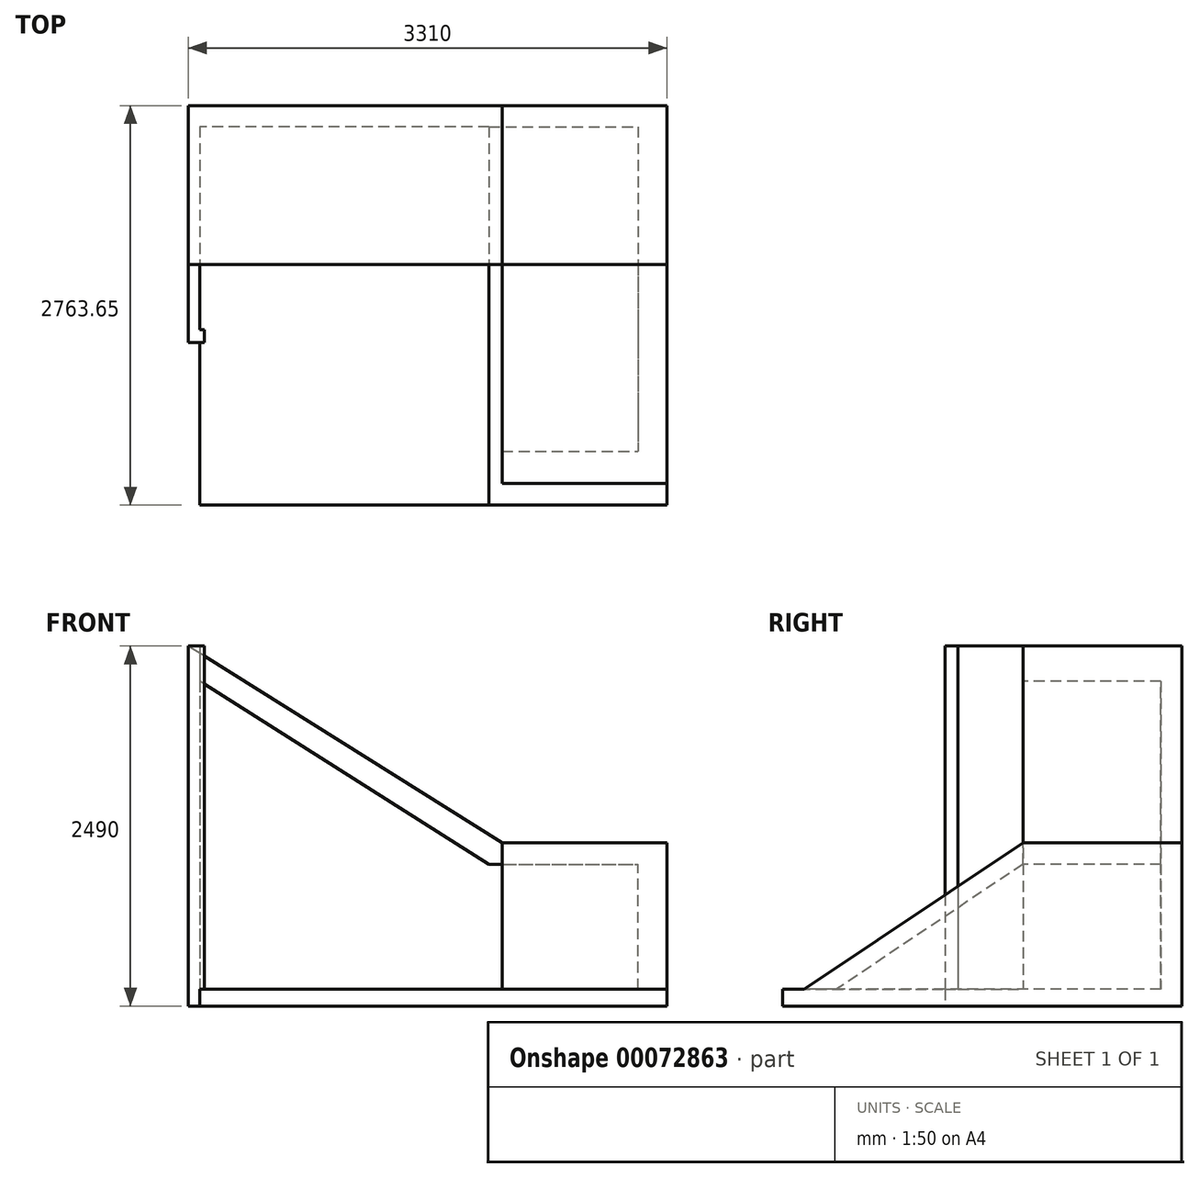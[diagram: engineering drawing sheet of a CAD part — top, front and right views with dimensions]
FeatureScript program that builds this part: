
annotation { "Feature Type Name" : "Feature", "Feature Type Description" : "" }
export const myFeature = defineFeature(function(context is Context, id is Id, definition is map)
    precondition{}
    {
        {
            var Q0;
            Q0=qCreatedBy(makeId("Front.planeOp"),FACE);
            var sketch = newSketch(context, id + "F0", { "sketchPlane" : qUnion([Q0])});
            skLineSegment(sketch, "E0", {"start": v(0, 0) * mm, "end": v(0, -2490) * mm});
            skLineSegment(sketch, "E1", {"start": v(0, -2490) * mm, "end": v(2170, -2490) * mm});
            skLineSegment(sketch, "E2", {"start": v(2170, -2490) * mm, "end": v(2170, -1360) * mm});
            skLineSegment(sketch, "E3", {"start": v(2170, -1360) * mm, "end": v(0, 0) * mm});
            skSolve(sketch);
        }
        {
            var Q0;
            Q0=makeQuery(id+"F0.imprint","IMPRINT",FACE,{"disambiguationData":[TD([[makeQuery(id+"F0.imprint","IMPRINT",EDGE,{"derivedFrom":sQuery(id+"F0.wireOp",EDGE,"E0")}),1.0]])]});
            extrude(context, id + "F1", {"entities" : qUnion([Q0]), "depth" : 1100 * mm});
        }
        {
            var Q0;
            Q0=makeQuery(id+"F1.opExtrude","CAP_FACE",FACE,{"disambiguationData":[OSD([sQuery(id+"F0.wireOp",EDGE,"E0"),sQuery(id+"F0.wireOp",EDGE,"E1"),sQuery(id+"F0.wireOp",EDGE,"E2"),sQuery(id+"F0.wireOp",EDGE,"E3")])],"isStart":false});
            var sketch = newSketch(context, id + "F2", { "sketchPlane" : qUnion([Q0])});
            skLineSegment(sketch, "E4", {"start": v(79.81, -244.3) * mm, "end": v(79.81, -2374.3) * mm});
            skLineSegment(sketch, "E5", {"start": v(79.81, -2374.3) * mm, "end": v(2079.81, -2374.3) * mm});
            skLineSegment(sketch, "E6", {"start": v(2079.81, -2374.3) * mm, "end": v(2079.81, -1509.3) * mm});
            skLineSegment(sketch, "E7", {"start": v(2079.81, -1509.3) * mm, "end": v(79.81, -244.3) * mm});
            skSolve(sketch);
        }
        {
            var Q0;
            Q0=makeQuery(id+"F2.imprint","IMPRINT",FACE,{"disambiguationData":[TD([[makeQuery(id+"F2.imprint","IMPRINT",EDGE,{"derivedFrom":sQuery(id+"F2.wireOp",EDGE,"E4")}),1.0]])]});
            extrude(context, id + "F3", {"entities" : qUnion([Q0]), "operationType" : NewBodyOperationType.REMOVE, "oppositeDirection" : true, "depth" : 955 * mm});
        }
        {
            var Q0;
            Q0=makeQuery(id+"F1.opExtrude","SWEPT_FACE",FACE,{"disambiguationData":[OSD([sQuery(id+"F0.wireOp",EDGE,"E0")])]});
            var sketch = newSketch(context, id + "F4", { "sketchPlane" : qUnion([Q0])});
            skLineSegment(sketch, "E8.bottom", {"start": v(1100, 0) * mm, "end": v(1550, 0) * mm});
            skLineSegment(sketch, "E8.top", {"start": v(1100, -2490) * mm, "end": v(1550, -2490) * mm});
            skLineSegment(sketch, "E8.left", {"start": v(1100, 0) * mm, "end": v(1100, -2490) * mm});
            skLineSegment(sketch, "E8.right", {"start": v(1550, 0) * mm, "end": v(1550, -2490) * mm});
            skSolve(sketch);
        }
        {
            var Q0;
            Q0=makeQuery(id+"F4.imprint","IMPRINT",FACE,{"disambiguationData":[TD([[makeQuery(id+"F4.imprint","IMPRINT",EDGE,{"derivedFrom":sQuery(id+"F4.wireOp",EDGE,"E8.bottom")}),-1.0]])]});
            extrude(context, id + "F5", {"entities" : qUnion([Q0]), "operationType" : NewBodyOperationType.ADD, "oppositeDirection" : true, "depth" : 80 * mm});
        }
        {
            var Q0;
            Q0=makeQuery(id+"F5.boolean.opBoolean","MERGE",FACE,{"derivedFrom":[makeQuery(id+"F1.opExtrude","SWEPT_FACE",FACE,{"disambiguationData":[OSD([sQuery(id+"F0.wireOp",EDGE,"E0")])]}),makeQuery(id+"F5.opExtrude","CAP_FACE",FACE,{"disambiguationData":[OSD([sQuery(id+"F4.wireOp",EDGE,"E8.bottom"),sQuery(id+"F4.wireOp",EDGE,"E8.top"),sQuery(id+"F4.wireOp",EDGE,"E8.left"),sQuery(id+"F4.wireOp",EDGE,"E8.right")])],"isStart":true})]});
            var sketch = newSketch(context, id + "F6", { "sketchPlane" : qUnion([Q0])});
            skLineSegment(sketch, "E9.bottom", {"start": v(1550, 0) * mm, "end": v(1640, 0) * mm});
            skLineSegment(sketch, "E9.top", {"start": v(1550, -2490) * mm, "end": v(1640, -2490) * mm});
            skLineSegment(sketch, "E9.left", {"start": v(1550, 0) * mm, "end": v(1550, -2490) * mm});
            skLineSegment(sketch, "E9.right", {"start": v(1640, 0) * mm, "end": v(1640, -2490) * mm});
            skSolve(sketch);
        }
        {
            var Q0;
            Q0=makeQuery(id+"F6.imprint","IMPRINT",FACE,{"disambiguationData":[TD([[makeQuery(id+"F6.imprint","IMPRINT",EDGE,{"derivedFrom":sQuery(id+"F6.wireOp",EDGE,"E9.bottom")}),-1.0]])]});
            extrude(context, id + "F7", {"entities" : qUnion([Q0]), "operationType" : NewBodyOperationType.ADD, "oppositeDirection" : true, "depth" : 110 * mm});
        }
        {
            var Q0;
            Q0=makeQuery(id+"F1.opExtrude","CAP_FACE",FACE,{"disambiguationData":[OSD([sQuery(id+"F0.wireOp",EDGE,"E0"),sQuery(id+"F0.wireOp",EDGE,"E1"),sQuery(id+"F0.wireOp",EDGE,"E2"),sQuery(id+"F0.wireOp",EDGE,"E3")])],"isStart":false});
            var sketch = newSketch(context, id + "F8", { "sketchPlane" : qUnion([Q0])});
            skLineSegment(sketch, "E10.bottom", {"start": v(2079.81, -1509.3) * mm, "end": v(2170, -1509.3) * mm});
            skLineSegment(sketch, "E10.top", {"start": v(2079.81, -2374.27) * mm, "end": v(2170, -2374.27) * mm});
            skLineSegment(sketch, "E10.left", {"start": v(2079.81, -1509.3) * mm, "end": v(2079.81, -2374.27) * mm});
            skLineSegment(sketch, "E10.right", {"start": v(2170, -1509.3) * mm, "end": v(2170, -2374.27) * mm});
            skSolve(sketch);
        }
        {
            var Q0;
            Q0=makeQuery(id+"F8.imprint","IMPRINT",FACE,{"disambiguationData":[TD([[makeQuery(id+"F8.imprint","IMPRINT",EDGE,{"derivedFrom":sQuery(id+"F8.wireOp",EDGE,"E10.bottom")}),-1.0]])]});
            extrude(context, id + "F9", {"entities" : qUnion([Q0]), "operationType" : NewBodyOperationType.REMOVE, "oppositeDirection" : true, "depth" : 955 * mm});
        }
        {
            var Q0;
            Q0=makeQuery(id+"F1.opExtrude","SWEPT_FACE",FACE,{"disambiguationData":[OSD([sQuery(id+"F0.wireOp",EDGE,"E2")])]});
            extrude(context, id + "F10", {"entities" : qUnion([Q0]), "operationType" : NewBodyOperationType.ADD, "depth" : 940 * mm});
        }
        {
            var Q0;
            {var subQ0=sQuery(id+"F0.wireOp",EDGE,"E2");var subQ4=sQuery(id+"F0.wireOp",EDGE,"E1");var subQ5=makeQuery(id+"F1.opExtrude","SWEPT_FACE",FACE,{"disambiguationData":[OSD([subQ4])]});var subQ7=makeQuery(id+"F1.opExtrude","CAP_FACE",FACE,{"disambiguationData":[OSD([sQuery(id+"F0.wireOp",EDGE,"E0"),subQ4,subQ0,sQuery(id+"F0.wireOp",EDGE,"E3")])],"isStart":false});Q0=makeQuery(id+"F10.boolean.opBoolean","MERGE",FACE,{"derivedFrom":[makeQuery(id+"F9.boolean.opBoolean","SPLIT",FACE,{"disambiguationData":[TD([subQ5])],"derivedFrom":subQ7}),makeQuery(id+"F10.opExtrude","SWEPT_FACE",FACE,{"disambiguationData":[OSD([subQ0]),TDD([makeQuery(id+"F9.boolean.opBoolean","SPLIT",EDGE,{"disambiguationData":[TD([subQ5])],"derivedFrom":makeQuery(id+"F1.opExtrude","CAP_EDGE",EDGE,{"disambiguationData":[OSD([subQ0])],"isStart":false})})])]})]});}
            extrude(context, id + "F11", {"entities" : qUnion([Q0]), "operationType" : NewBodyOperationType.ADD, "depth" : 1290 * mm});
        }
        {
            var Q0;
            {var subQ0=sQuery(id+"F0.wireOp",EDGE,"E2");Q0=makeQuery(id+"F11.boolean.opBoolean","MERGE",FACE,{"derivedFrom":[makeQuery(id+"F10.opExtrude","CAP_FACE",FACE,{"disambiguationData":[OSD([subQ0])],"isStart":false}),makeQuery(id+"F11.opExtrude","SWEPT_FACE",FACE,{"disambiguationData":[OSD([subQ0])]})]});}
            var sketch = newSketch(context, id + "F12", { "sketchPlane" : qUnion([Q0])});
            skLineSegment(sketch, "E11", {"start": v(-1100, -1509.3) * mm, "end": v(-2390, -2374.27) * mm});
            skLineSegment(sketch, "E12", {"start": v(-1100, -1360) * mm, "end": v(-2619.97, -2379.18) * mm});
            skLineSegment(sketch, "E13", {"start": v(-2390, -2374.27) * mm, "end": v(-2619.97, -2379.18) * mm});
            skSolve(sketch);
        }
        {
            var Q0;
            Q0=makeQuery(id+"F12.imprint","IMPRINT",FACE,{"disambiguationData":[TD([[makeQuery(id+"F12.imprint","IMPRINT",EDGE,{"derivedFrom":sQuery(id+"F12.wireOp",EDGE,"E11")}),-1.0]])]});
            extrude(context, id + "F13", {"entities" : qUnion([Q0]), "oppositeDirection" : true, "depth" : 940 * mm});
        }
        {
            var Q0;
            Q0=makeQuery(id+"F11.opExtrude","CAP_FACE",FACE,{"disambiguationData":[OSD([sQuery(id+"F0.wireOp",EDGE,"E0"),sQuery(id+"F0.wireOp",EDGE,"E1"),sQuery(id+"F0.wireOp",EDGE,"E2"),sQuery(id+"F0.wireOp",EDGE,"E3")])],"isStart":false});
            extrude(context, id + "F14", {"entities" : qUnion([Q0]), "operationType" : NewBodyOperationType.ADD, "depth" : 373.65 * mm});
        }
        {
            var Q0;
            {var subQ0=sQuery(id+"F0.wireOp",EDGE,"E2");Q0=makeQuery(id+"F14.boolean.opBoolean","MERGE",FACE,{"derivedFrom":[makeQuery(id+"F11.boolean.opBoolean","MERGE",FACE,{"derivedFrom":[makeQuery(id+"F10.opExtrude","CAP_FACE",FACE,{"disambiguationData":[OSD([subQ0])],"isStart":false}),makeQuery(id+"F11.opExtrude","SWEPT_FACE",FACE,{"disambiguationData":[OSD([subQ0])]})]}),makeQuery(id+"F13.opExtrude","CAP_FACE",FACE,{"disambiguationData":[OSD([subQ0,sQuery(id+"F12.wireOp",EDGE,"E11"),sQuery(id+"F12.wireOp",EDGE,"E12"),sQuery(id+"F12.wireOp",EDGE,"E13")])],"isStart":true}),makeQuery(id+"F14.opExtrude","SWEPT_FACE",FACE,{"disambiguationData":[OSD([subQ0])]})]});}
            var sketch = newSketch(context, id + "F15", { "sketchPlane" : qUnion([Q0])});
            skLineSegment(sketch, "E14", {"start": v(0, -1360) * mm, "end": v(0, -2490) * mm});
            skLineSegment(sketch, "E15", {"start": v(0, -2490) * mm, "end": v(-2763.65, -2490) * mm});
            skLineSegment(sketch, "E16", {"start": v(-2763.65, -2490) * mm, "end": v(-2763.65, -2374.27) * mm});
            skLineSegment(sketch, "E17", {"start": v(-2763.65, -2374.27) * mm, "end": v(-2612.65, -2374.27) * mm});
            skLineSegment(sketch, "E18", {"start": v(-2612.65, -2374.27) * mm, "end": v(-1100, -1360) * mm});
            skLineSegment(sketch, "E19", {"start": v(-1100, -1360) * mm, "end": v(0, -1360) * mm});
            skSolve(sketch);
        }
        {
            var Q0;
            Q0=qSketchRegion(id+"F15",true);
            extrude(context, id + "F16", {"entities" : qUnion([Q0]), "operationType" : NewBodyOperationType.ADD, "depth" : 200 * mm});
        }
    });
